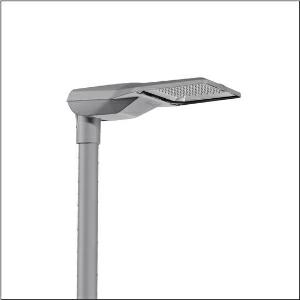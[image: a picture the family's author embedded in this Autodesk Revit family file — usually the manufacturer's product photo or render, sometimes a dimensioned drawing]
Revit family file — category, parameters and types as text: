
# Revit family: streetlight_sl_21_iq_midi___st1_5a_5xe3p41g08mb_0a3d
name_source: partatom
category: Lighting Fixtures
units: mm (PartAtom-declared; Revit-internal decimal feet)

## family parameters
Cut with Voids When Loaded = No
Host = Face
Light Source = No
Part Type = Normal
Room Calculation Point = No
Round Connector Dimension = Use Diameter
Shared = No

## types (1)
- --- (1 x LED, 20000 lm, 146.7 W, 4000K)
    Apparent Load = 147 VA
    CIE Flux Codes = 22 53 95 100 100
    Color Rendering = 70
    Color Temperature = 4000K
    Default Elevation = 1800 mm
    Description = Streetlight SL 21 iQ midi, mast luminaire, primary light control with lens, of PMMA, primary optical cover: cover, of toughened safety glass, transparent, light distribution: ST1.5a, light emission: direct distribution, primary light characteristic: asymmetric, installation type: post-top, side-entry, LED, High Power LED, rated luminous flux: 20.000lm, luminous efficacy: 136lm/W, light colour: 740, colour temperature: 4000K, control: Street-Remote, Auto-Match, Temp-Guard, Lumen-Switch, Night-Set, Smart-Wire, Light-Fading, Desk-Remote (wireless, voltage-free reading and setting of iQ features in the workshop via application-optimized NFC function/RFID function), optimised constant luminous flux control (CLO 2.0), presetting dimming linear, mains connection: 230..240V, AC, 50/60Hz, start of lifetime: 147W, end of service life: 161W, reduction: 62W, luminaire housing, of diecast aluminium, powder-coated, Siteco® metallic grey (DB 702S), corrosivity category C5 mid according to DIN EN ISO 12944, please order mast flange separately, inclination adjustable: 0°, 5°, 10°, 15°, sealing non-destructively replaceable, multi-level sealing system, length: 644mm, width: 335mm, height: 110mm, mast flange for spigot size: 42mm (side-entry): 5XC10008XM4, 60/48mm (side-entry/post-top): 5XC10108XM2, 76/60mm (side-entry/post-top): 5XC10108XM1, protection rating (complete): IP66, insulation class (complete): insulation class II (safety insulation), certification: CE, ENEC, ENEC+, VDE, impact resistance: IK09, permissible operating ambient temperature for outdoor applications: -40..+50°C, standard-compliant lighting for roads and squares, packaging unit: 1 piece

Light Distribution: ST1.5a
    Height = 111 mm
    Lamp = 1 x LED
    Lamp Light Flux = 20000 lm
    Lamp Power = 146.7 W
    Lamp count = 1
    Length = 644 mm
    Luminous efficacy = 136 lm/W
    Manufacturer = Siteco
    ModVariant = No
    Model = 5XE3P41G08MB
    Number of Poles = 1
    OnlyDefault = Yes
    Power Factor = 1
    Product Name = Streetlight SL 21 iQ midi | ST1.5a
    Product group = mast luminaire | pylon top
    ProductGroupID = 6100
    Protection Class = Protection class II
    Protection Degree = IP 66
    RLX_Detail_Level = 1
    RLX_Emergency_Light_Flux = 0 lm
    RLX_Emergency_Type = 0
    RLX_Emergency_Type_DB = No
    RlxData = <blob elided: 94153 chars, md5=8d72d077>
    Socket = socket
    Standby Power = 0 W
    System Light Flux = 20000 lm
    System Power = 147 W
    Type Comments = factory setting: luminous flux: 100 % | dim-lin: 254 | 753 mA
    Type Image = l_1004298.jpg
    URL = http://relux.com
    VarID = @adj_109585
    Voltage = 0 V
    Weight = 0.00 kg
    Width = 336 mm

## geometry (parser evidence)
native form markers: Blend x4, Sweep x10
no freeform markers — native parametric forms only
